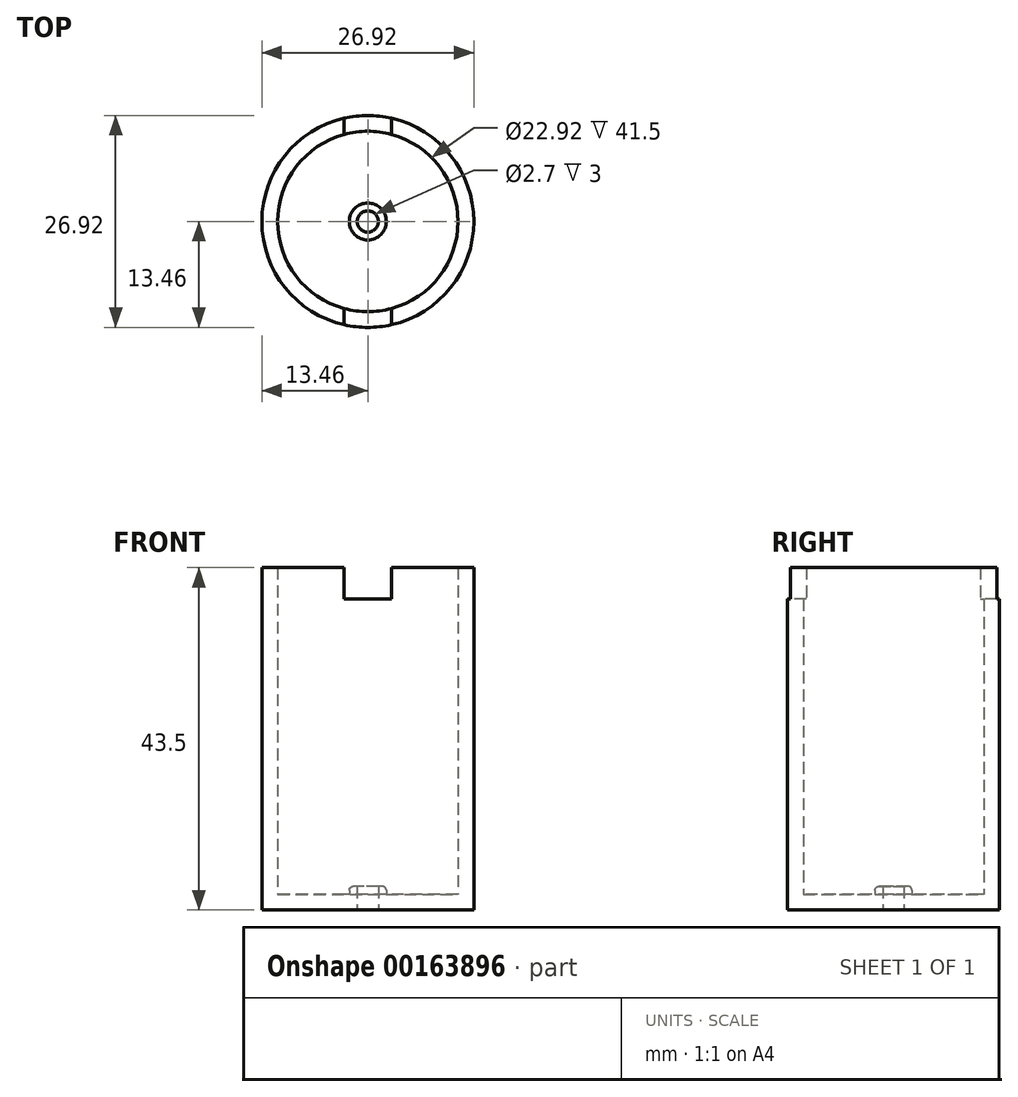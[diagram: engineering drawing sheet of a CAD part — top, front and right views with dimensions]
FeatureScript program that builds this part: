
annotation { "Feature Type Name" : "Feature", "Feature Type Description" : "" }
export const myFeature = defineFeature(function(context is Context, id is Id, definition is map)
    precondition{}
    {
        {
            var Q0;
            Q0=qCreatedBy(makeId("Top.planeOp"),FACE);
            var sketch = newSketch(context, id + "F0", { "sketchPlane" : qUnion([Q0])});
            skCircle(sketch, "E0", {"center": v(0, 0) * mm, "radius": 13.46 * mm});
            skSolve(sketch);
        }
        {
            var Q0;
            Q0=makeQuery(id+"F0.imprint","IMPRINT",FACE,{"disambiguationData":[TD([[makeQuery(id+"F0.imprint","IMPRINT",EDGE,{"derivedFrom":sQuery(id+"F0.wireOp",EDGE,"E0")}),1.0]])]});
            extrude(context, id + "F1", {"entities" : qUnion([Q0]), "depth" : 43.5 * mm});
        }
        {
            var Q0;
            Q0=makeQuery(id+"F1.opExtrude","CAP_FACE",FACE,{"disambiguationData":[OSD([sQuery(id+"F0.wireOp",EDGE,"E0")])],"isStart":false});
            shell(context, id + "F2", {"entities" : qUnion([Q0]), "thickness" : 2 * mm});
        }
        {
            var Q0;
            Q0=makeQuery(id+"F1.opExtrude","CAP_FACE",FACE,{"disambiguationData":[OSD([sQuery(id+"F0.wireOp",EDGE,"E0")])],"isStart":false});
            var sketch = newSketch(context, id + "F3", { "sketchPlane" : qUnion([Q0])});
            skLineSegment(sketch, "E1.bottom", {"start": v(3, 15) * mm, "end": v(-3, 15) * mm});
            skLineSegment(sketch, "E1.top", {"start": v(3, -15) * mm, "end": v(-3, -15) * mm});
            skLineSegment(sketch, "E1.left", {"start": v(3, 15) * mm, "end": v(3, -15) * mm});
            skLineSegment(sketch, "E1.right", {"start": v(-3, 15) * mm, "end": v(-3, -15) * mm});
            skPoint(sketch, "E1.middle", {"position": v(0, 0) * mm});
            skSolve(sketch);
        }
        {
            var Q0;
            Q0 = qSketchRegion(id + "F3", true);
            extrude(context, id + "F4", {"entities" : qUnion([Q0]), "operationType" : NewBodyOperationType.REMOVE, "oppositeDirection" : true, "depth" : 4 * mm});
        }
        {
            var Q0;
            Q0=makeQuery(id+"F1.opExtrude","CAP_FACE",FACE,{"disambiguationData":[OSD([sQuery(id+"F0.wireOp",EDGE,"E0")])],"isStart":true});
            var sketch = newSketch(context, id + "F5", { "sketchPlane" : qUnion([Q0])});
            skCircle(sketch, "E2", {"center": v(0, 0) * mm, "radius": 1.35 * mm});
            skSolve(sketch);
        }
        {
            var Q0;
            Q0 = qSketchRegion(id + "F5", true);
            extrude(context, id + "F6", {"entities" : qUnion([Q0]), "operationType" : NewBodyOperationType.REMOVE, "endBound" : BoundingType.THROUGH_ALL, "oppositeDirection" : true, "depth" : 25 * mm});
        }
        {
            var Q0;
            {var subQ0=sQuery(id+"F0.wireOp",EDGE,"E0");Q0=makeQuery(id+"F2.opShell","OFFSET_FACE",FACE,{"disambiguationData":[OSD([subQ0]),TDD([makeQuery(id+"F1.opExtrude","CAP_FACE",FACE,{"disambiguationData":[OSD([subQ0])],"isStart":true})])]});}
            var sketch = newSketch(context, id + "F7", { "sketchPlane" : qUnion([Q0])});
            skCircle(sketch, "E3.0", {"center": v(0, 0) * mm, "radius": 1.35 * mm});
            skCircle(sketch, "E4.0", {"center": v(0, 0) * mm, "radius": 2.35 * mm});
            skCircle(sketch, "E5.0", {"center": v(0, 0) * mm, "radius": 16.46 * mm});
            skSolve(sketch);
        }
        {
            var Q0;
            Q0=makeQuery(id+"F7.imprint","IMPRINT",FACE,{"disambiguationData":[TD([[makeQuery(id+"F7.imprint","IMPRINT",EDGE,{"derivedFrom":sQuery(id+"F7.wireOp",EDGE,"E3.0")}),-1.0]])]});
            extrude(context, id + "F8", {"entities" : qUnion([Q0]), "operationType" : NewBodyOperationType.ADD, "depth" : 1 * mm});
        }
        {
            var Q0;
            Q0=makeQuery(id+"F8.opExtrude","CAP_EDGE",EDGE,{"disambiguationData":[OSD([sQuery(id+"F7.wireOp",EDGE,"E4.0")])],"isStart":false});
            fillet(context, id + "F9", {"entities" : qUnion([Q0]), "radius" : .5 * mm, "tangentPropagation" : true, "allowEdgeOverflow" : false});
        }
    });
